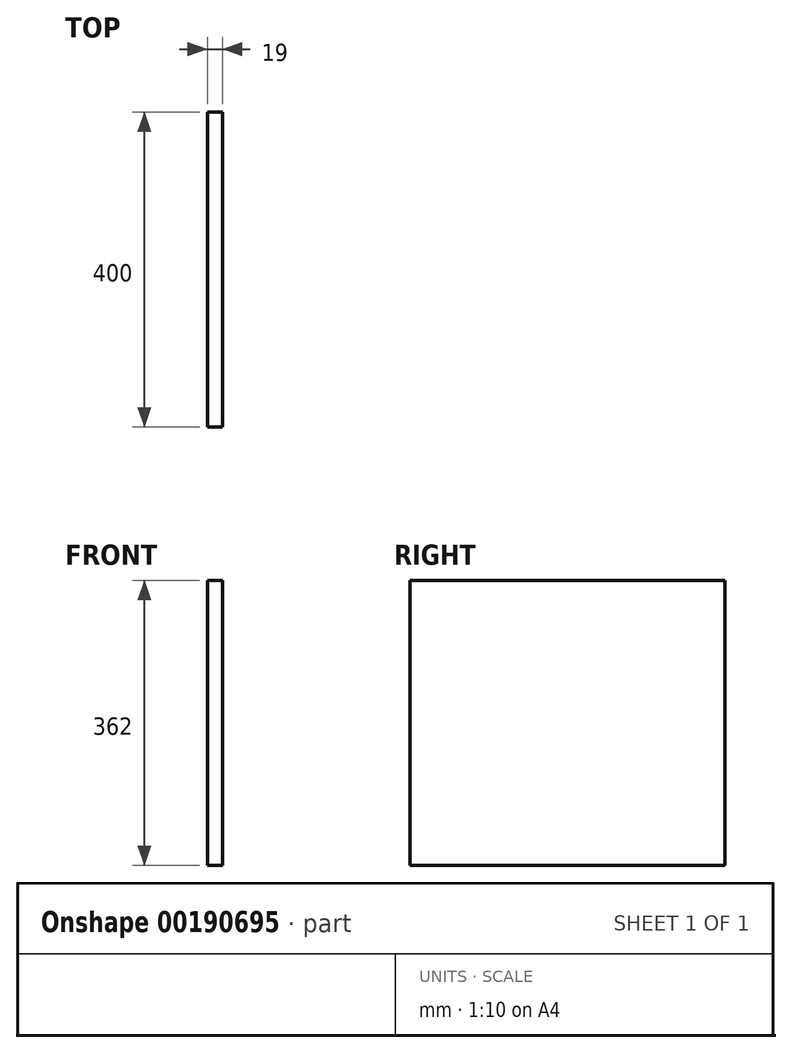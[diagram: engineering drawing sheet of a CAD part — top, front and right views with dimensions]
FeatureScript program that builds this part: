
annotation { "Feature Type Name" : "Feature", "Feature Type Description" : "" }
export const myFeature = defineFeature(function(context is Context, id is Id, definition is map)
    precondition{}
    {
        {
            var Q0;
            Q0=qCreatedBy(makeId("Right.planeOp"),FACE);
            var sketch = newSketch(context, id + "F0", { "sketchPlane" : qUnion([Q0])});
            skLineSegment(sketch, "E0.bottom", {"start": v(-160.37, 178.3) * mm, "end": v(239.63, 178.3) * mm});
            skLineSegment(sketch, "E0.top", {"start": v(-160.37, -183.7) * mm, "end": v(239.63, -183.7) * mm});
            skLineSegment(sketch, "E0.left", {"start": v(-160.37, 178.3) * mm, "end": v(-160.37, -183.7) * mm});
            skLineSegment(sketch, "E0.right", {"start": v(239.63, 178.3) * mm, "end": v(239.63, -183.7) * mm});
            skSolve(sketch);
        }
        {
            var Q0;
            Q0 = qSketchRegion(id + "F0", true);
            extrude(context, id + "F1", {"entities" : qUnion([Q0]), "depth" : 19 * mm});
        }
    });
